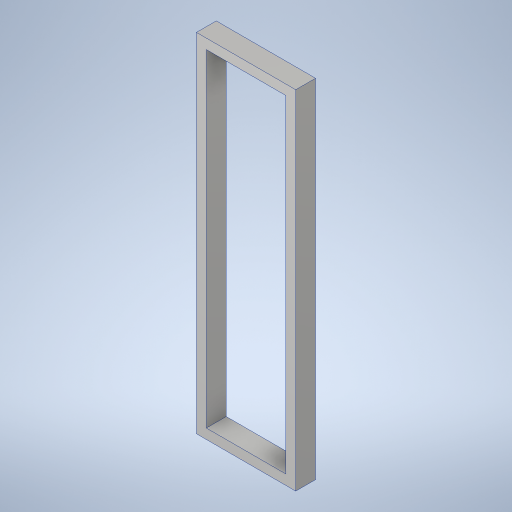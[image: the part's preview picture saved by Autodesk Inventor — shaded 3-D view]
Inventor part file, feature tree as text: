
AUTODESK INVENTOR PART (.ipt)
format: ipt  version: 2023.4 (Build 274418000, 418)  size: 238,080 bytes
history: native  units: in
note: dims shown in document units (in); Inventor stores cm internally (conversion verified against a paired STEP export)
features: extrude x1, sketch x1
ambient origin geometry x8: Origin, YZ Plane, XZ Plane, XY Plane, X Axis, Y Axis, Z Axis, Center Point
bodies: Solid1 (feature_tree)
feature tree (2):
  extrude  "Extrusion1"  Depth=35.0in
  sketch  "Sketch1"  dims[d0=10.0in d1=35.0in d2=2.0in d3=0.0in d4=1.0in]
